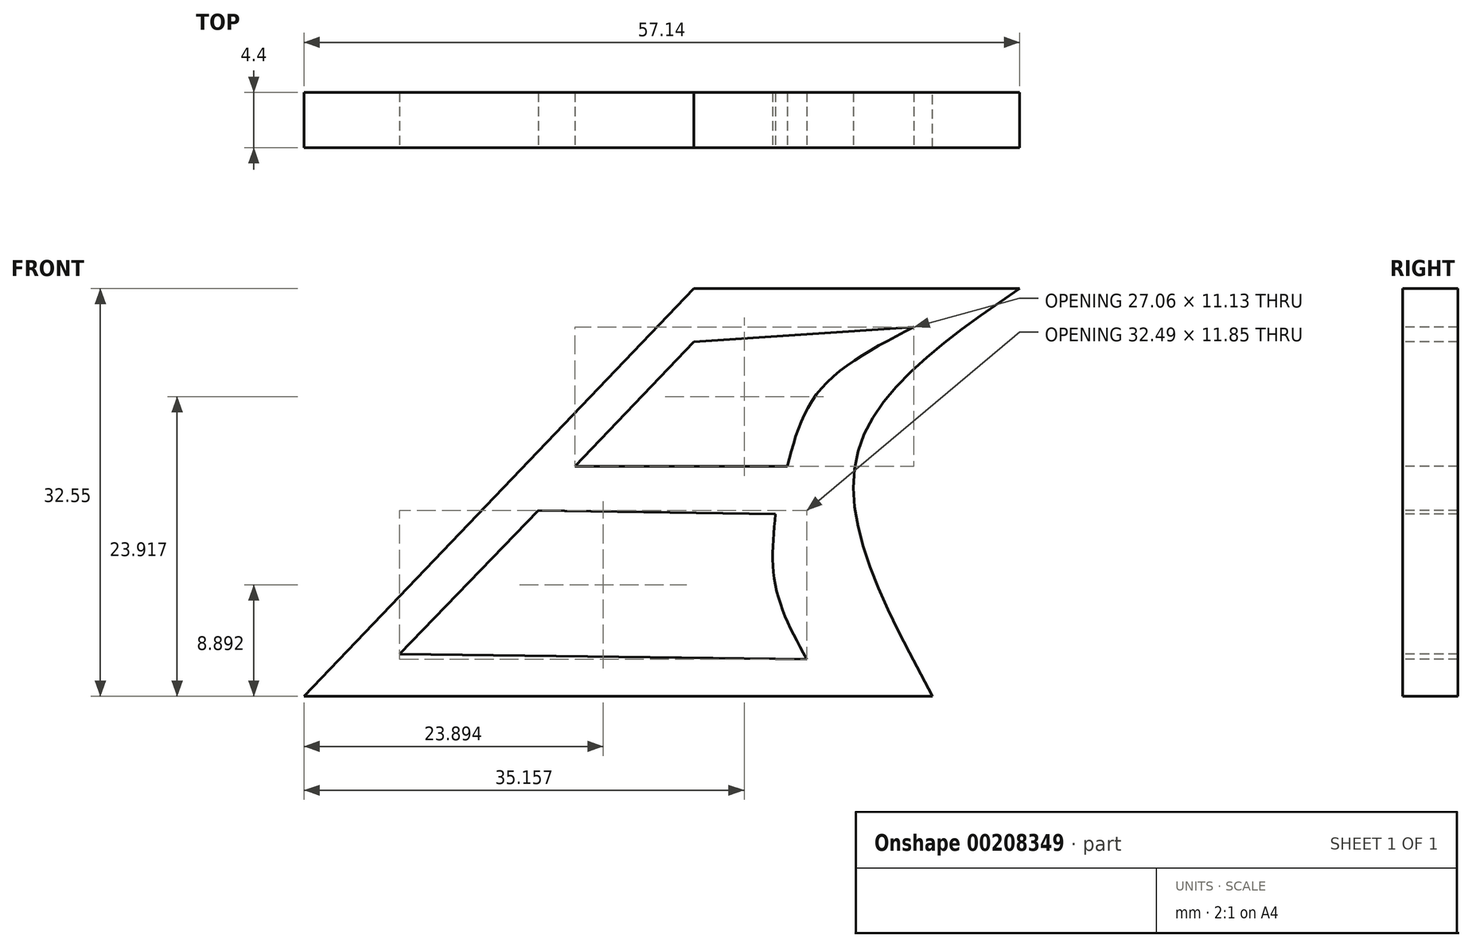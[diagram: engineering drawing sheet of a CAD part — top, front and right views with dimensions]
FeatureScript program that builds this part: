
annotation { "Feature Type Name" : "Feature", "Feature Type Description" : "" }
export const myFeature = defineFeature(function(context is Context, id is Id, definition is map)
    precondition{}
    {
        {
            var Q0;
            Q0=qCreatedBy(makeId("Front.planeOp"),FACE);
            var sketch = newSketch(context, id + "F0", { "sketchPlane" : qUnion([Q0])});
            skLineSegment(sketch, "E0", {"start": v(0, 0) * mm, "end": v(31.12, 32.55) * mm});
            skLineSegment(sketch, "E1", {"start": v(31.12, 32.55) * mm, "end": v(57.14, 32.55) * mm});
            skPoint(sketch, "E2.1.internal.snap0", {"position": v(44.13, 32.55) * mm});
            skFitSpline(sketch, "E2", {"points": [v(57.14, 32.55) * mm, v(44.13, 19.14) * mm, v(50.2, 0) * mm], "startDerivative": vector(-35.92, -24.79) * mm, "endDerivative": vector(21.7, -40.22) * mm});
            skLineSegment(sketch, "E3", {"start": v(50.2, 0) * mm, "end": v(0, 0) * mm});
            skSolve(sketch);
        }
        {
            var Q0;
            Q0 = qSketchRegion(id + "F0", true);
            extrude(context, id + "F4", {"entities" : qUnion([Q0]), "depth" : 4.4 * mm});
        }
        {
            var Q0;
            Q0=makeQuery(id+"F4.opExtrude","CAP_FACE",FACE,{"disambiguationData":[OSD([sQuery(id+"F0.wireOp",EDGE,"E0"),sQuery(id+"F0.wireOp",EDGE,"E1"),sQuery(id+"F0.wireOp",EDGE,"E2"),sQuery(id+"F0.wireOp",EDGE,"E3")])],"isStart":false});
            var sketch = newSketch(context, id + "F5", { "sketchPlane" : qUnion([Q0])});
            skLineSegment(sketch, "E4", {"start": v(31.12, 28.28) * mm, "end": v(21.63, 18.35) * mm});
            skLineSegment(sketch, "E5", {"start": v(21.63, 18.35) * mm, "end": v(38.6, 18.35) * mm});
            skFitSpline(sketch, "E6", {"points": [v(38.6, 18.35) * mm, v(41.12, 24.36) * mm, v(48.69, 29.48) * mm], "startDerivative": vector(3.55, 13.96) * mm, "endDerivative": vector(16.26, 8.46) * mm});
            skLineSegment(sketch, "E7", {"start": v(31.12, 28.28) * mm, "end": v(48.69, 29.48) * mm});
            skSolve(sketch);
        }
        {
            var Q0;
            Q0 = qSketchRegion(id + "F5", true);
            extrude(context, id + "F1", {"entities" : qUnion([Q0]), "operationType" : NewBodyOperationType.REMOVE, "oppositeDirection" : true, "depth" : 25.4 * mm});
        }
        {
            var Q0;
            Q0=makeQuery(id+"F4.opExtrude","CAP_FACE",FACE,{"disambiguationData":[OSD([sQuery(id+"F0.wireOp",EDGE,"E0"),sQuery(id+"F0.wireOp",EDGE,"E1"),sQuery(id+"F0.wireOp",EDGE,"E2"),sQuery(id+"F0.wireOp",EDGE,"E3")])],"isStart":false});
            var sketch = newSketch(context, id + "F2", { "sketchPlane" : qUnion([Q0])});
            skLineSegment(sketch, "E8", {"start": v(18.73, 14.82) * mm, "end": v(7.65, 3.37) * mm});
            skLineSegment(sketch, "E9", {"start": v(7.65, 3.37) * mm, "end": v(40.14, 2.97) * mm});
            skFitSpline(sketch, "E10", {"points": [v(40.14, 2.97) * mm, v(37.66, 8.77) * mm, v(37.65, 14.55) * mm], "startDerivative": vector(-6.1, 11.24) * mm, "endDerivative": vector(1.17, 11.94) * mm});
            skLineSegment(sketch, "E11", {"start": v(18.73, 14.82) * mm, "end": v(37.65, 14.55) * mm});
            skSolve(sketch);
        }
        {
            var Q0;
            Q0 = qSketchRegion(id + "F2", true);
            extrude(context, id + "F3", {"entities" : qUnion([Q0]), "operationType" : NewBodyOperationType.REMOVE, "oppositeDirection" : true, "depth" : 25.4 * mm});
        }
    });
